# Revit family: IS_Strada_A6450_BIM_DE
name_source: partatom
category: Plumbing Fixtures
revit_build: Autodesk Revit MEP 2016 (Build: 20161004_0715(x64)
units: mm (PartAtom-declared; Revit-internal decimal feet)

## family parameters
Always vertical = No
Cut with Voids When Loaded = No
OmniClass Number = 23.45.55.17
OmniClass Title = Mixing Faucets
Part Type = Normal
Room Calculation Point = No
Round Connector Dimension = Use Diameter
Shared = No
Work Plane-Based = No

## types (1)
- A6450AA - STRADA single lever one hole basin mixer, no pop-up waste
    Accessories = www.idealstandard.de\ersatzteile
    AreaUnits = millimeters
    AssetType = Fixed
    BIMObjectName = ISI_IdealStandard_
    BIMobject category = Basins
    BOSUseNativeGeometries = 1
    BarCode = 4015413332279
    Brand = Ideal Standard
    Brand url = http://www.idealstandard.co.uk
    CodePerformance = 0
    Color = Chrome
    ConnectionType = Plumbing
    Cost = 0 $
    CurrencyUnit = €
    CurrentRevision = 1
    Date of publishing = 43049
    Description = IS Waschtischarmatur STRADA, 5 l/min., o.Ablgarn., Ausld. 113mm, Chrom
    DurationUnit = year
    EAN code = https://4015413332279
    Edition number = 1
    ExpectedLife = 25
    FaucetFunction = mixed
    FaucetOperation = leverhandle
    FaucetType = pillar
    Features = STRADA single lever one hole basin mixer, no pop-up waste
    Finish = Chrome
    IFC Classification = Sanitary Terminal
    IfcExportAs = Ifc Valve Type
    Installation instructions = http://www.idealstandard.de
    InstallationInstructions = www.idealstandard.de\produkte
    LinearUnits = millimeters
    MainColor = Chrome
    MaintenanceInformation = www.idealstandard.de\produkte
    Manufacturer name = Ideal Standard
    ManufacturerURL = http://www.idealstandard.com
    Material = Brass
    Material main = Brass
    Model = A6450AA
    ModelNumber = A6450AA
    ModelReference = IS Waschtischarmatur STRADA, 5 l/min., o.Ablgarn., Ausld. 113mm, Chrom
    NettWeight = 2,216 kg
    Nominal height = 154
    Nominal width = 51
    NominalDepth = 159 mm  [stored 0.521654 ft]
    NominalHeight = 154 mm  [stored 0.505249 ft]
    NominalLength = 159 mm  [stored 0.521654 ft]
    NominalWidth = 51 mm  [stored 0.167323 ft]
    Product Guid = 57f5b564-bbdf-4027-8f77-81c894a4c741
    Product SKU = A6450
    Product data url = https://bimobject.com
    Product family = STRADA
    Product group = Basin Mixer
    Product name = STRADA single lever one hole basin mixer, no pop-up waste
    Product url = http://www.idealstandard.de
    ProductInformation = http://www.idealstandard.de
    QR code = http://bimobject.com
    Shape = Sculptured
    Size = 154 x 159 x 51mm
    Space = Internal
    SpareParts = www.idealstandard.de/ersatzteile
    Technical description = http://www.idealstandard.de
    TestPressure = 10 Bar
    URL = http://www.idealstandard.de
    Uniclass2015Version = Products v1.1
    ValveMechanism = ceramic disc
    ValveOperation = lever
    Version = 1
    VolumeUnits = Litres
    Weight Net (Kg) = 2.22
    WorkingPressure = 1-5 Bar

note: [stored X ft] marks values corroborated as IEEE doubles in the binary element streams (Revit-internal decimal feet)

## geometry (parser evidence)
native form markers: Blend x4, Sweep x1
no freeform markers — native parametric forms only
